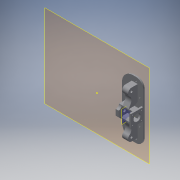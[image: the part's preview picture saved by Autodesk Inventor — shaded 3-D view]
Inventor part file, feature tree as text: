
AUTODESK INVENTOR PART (.ipt)
format: ipt  version: 2016 (Build 200138000, 138)  size: 395,776 bytes
history: native  units: in
note: dims shown in document units (in); Inventor stores cm internally (conversion verified against a paired STEP export)
features: sketch x11, extrude x9, projected_geometry x6, fillet x3, plane x2, chamfer x1, reference x1
ambient origin geometry x8: Origin, YZ Plane, XZ Plane, XY Plane, X Axis, Y Axis, Z Axis, Center Point
bodies: Solid1 (feature_tree)
feature tree (33):
  plane  "Work Plane1"
  extrude  "Extrusion1"  Depth=0.2in TaperAngle=0.0deg
  extrude  "Extrusion2"  TaperAngle=90.0deg  [1 undecoded]
  extrude  "Extrusion3"  Depth=1.7in
  extrude  "Extrusion4"  Depth=0.6102in
  extrude  "Extrusion5"  Depth=0.1181in
  extrude  "Extrusion6"  Depth=0.2362in TaperAngle=0.0deg
  extrude  "Extrusion7"  Depth=0.8in
  plane  "Work Plane2"
  extrude  "Extrusion8"  Depth=1.4961in TaperAngle=0.0deg
  extrude  "Extrusion9"  Depth=0.3937in TaperAngle=0.0deg
  fillet  "Fillet1"  Radius=0.45in
  fillet  "Fillet2"  Radius=0.45in
  fillet  "Fillet3"  Radius=0.45in
  sketch  "Sketch10"  dims[d33=0.45in d34=0.8312in d35=0.0in]
  sketch  "Sketch11"  dims[d36=0.3937in d37=0.0787in d38=0.0in d39=0.4537in d40=0.0in d41=0.9375in d42=0.8287in d43=0.0in d45=2.7559in d46=0.315in d47=2.7559in d48=0.315in d49=1.0in d50=1.0in d51=0.8287in d52=0.0in d53=1.5625in d54=1.0in d55=0.8125in d56=0.1875in d57=0.125in d58=45.0deg]
  chamfer  "Chamfer1"  Distance=0.8312in
  sketch  "Sketch1"  dims[d0=8.0in d1=0.2in d2=0.0in]
  reference  "Reference1"
  sketch  "Sketch2"  dims[d3=0.85in d4=90.0deg]
  projected_geometry  "Projected Loop1"
  sketch  "Sketch3"  dims[d5=1.7in d6=1.7in]
  projected_geometry  "Projected Loop2"
  sketch  "Sketch4"  dims[d7=0.9843in d8=0.6102in]
  projected_geometry  "Projected Loop3"
  sketch  "Sketch5"  dims[d9=0.6102in d10=0.1181in]
  projected_geometry  "Projected Loop4"
  sketch  "Sketch6"  dims[d11=0.7874in d13=1.2205in d14=0.7874in d16=1.2205in d19=0.2362in d20=0.0in]
  projected_geometry  "Projected Loop5"
  sketch  "Sketch7"  dims[d21=0.8in d22=0.8in]
  projected_geometry  "Projected Loop6"
  sketch  "Sketch8"  dims[d23=0.8in d24=1.4961in d25=0.0in]
  sketch  "Sketch9"  dims[d26=0.8661in d27=0.3937in d28=0.0in d30=0.45in d31=0.45in d32=0.45in]
note: 1 required parameter value undecoded (feature->parameter linkage not recoverable at this tier; creation-order binding heuristic only, values carry confidence <= 0.55)
